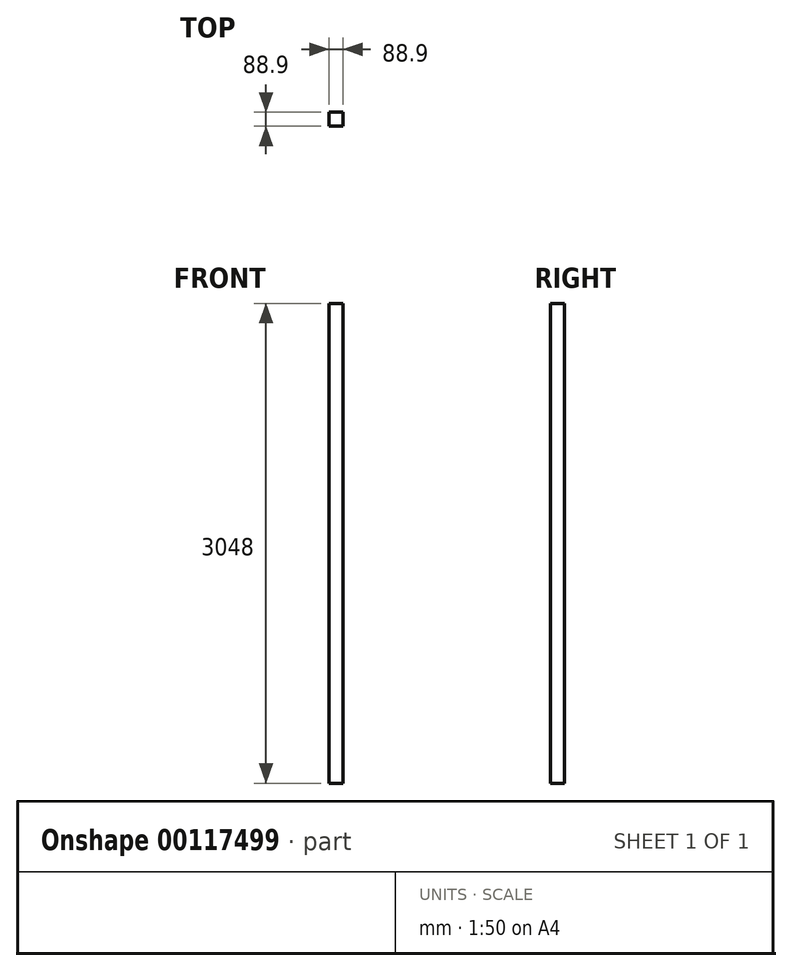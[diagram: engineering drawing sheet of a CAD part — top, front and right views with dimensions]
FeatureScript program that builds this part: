
annotation { "Feature Type Name" : "Feature", "Feature Type Description" : "" }
export const myFeature = defineFeature(function(context is Context, id is Id, definition is map)
    precondition{}
    {
        {
            var Q0;
            Q0=qCreatedBy(makeId("Top.planeOp"),FACE);
            var sketch = newSketch(context, id + "F0", { "sketchPlane" : qUnion([Q0])});
            skLineSegment(sketch, "E0.bottom", {"start": v(0, 0) * mm, "end": v(88.9, 0) * mm});
            skLineSegment(sketch, "E0.top", {"start": v(0, 88.9) * mm, "end": v(88.9, 88.9) * mm});
            skLineSegment(sketch, "E0.left", {"start": v(0, 0) * mm, "end": v(0, 88.9) * mm});
            skLineSegment(sketch, "E0.right", {"start": v(88.9, 0) * mm, "end": v(88.9, 88.9) * mm});
            skSolve(sketch);
        }
        {
            var Q0;
            Q0=makeQuery(id+"F0.imprint","IMPRINT",FACE,{"disambiguationData":[TD([[makeQuery(id+"F0.imprint","IMPRINT",EDGE,{"derivedFrom":sQuery(id+"F0.wireOp",EDGE,"E0.bottom")}),1.0]])]});
            extrude(context, id + "F1", {"entities" : qUnion([Q0]), "depth" : 3048 * mm});
        }
        {
            var Q0;
            Q0=qCreatedBy(makeId("Front.planeOp"),FACE);
            var sketch = newSketch(context, id + "F2", { "sketchPlane" : qUnion([Q0])});
            skLineSegment(sketch, "E1.bottom", {"start": v(-127.54, 0) * mm, "end": v(-165.64, 0) * mm});
            skLineSegment(sketch, "E1.top", {"start": v(-127.54, 184.15) * mm, "end": v(-165.64, 184.15) * mm});
            skLineSegment(sketch, "E1.left", {"start": v(-127.54, 0) * mm, "end": v(-127.54, 184.15) * mm});
            skLineSegment(sketch, "E1.right", {"start": v(-165.64, 0) * mm, "end": v(-165.64, 184.15) * mm});
            skSolve(sketch);
        }
        {
            var Q0;
            Q0=makeQuery(id+"F2.imprint","IMPRINT",FACE,{"disambiguationData":[TD([[makeQuery(id+"F2.imprint","IMPRINT",EDGE,{"derivedFrom":sQuery(id+"F2.wireOp",EDGE,"E1.bottom")}),-1.0]])]});
            extrude(context, id + "F3", {"entities" : qUnion([Q0]), "depth" : 2362.2 * mm});
        }
        {
            var Q0;
            Q0=qCreatedBy(makeId("Right.planeOp"),FACE);
            var sketch = newSketch(context, id + "F4", { "sketchPlane" : qUnion([Q0])});
            skLineSegment(sketch, "E2.bottom", {"start": v(230.04, 0) * mm, "end": v(268.14, 0) * mm});
            skLineSegment(sketch, "E2.top", {"start": v(230.04, 184.15) * mm, "end": v(268.14, 184.15) * mm});
            skLineSegment(sketch, "E2.left", {"start": v(230.04, 0) * mm, "end": v(230.04, 184.15) * mm});
            skLineSegment(sketch, "E2.right", {"start": v(268.14, 0) * mm, "end": v(268.14, 184.15) * mm});
            skSolve(sketch);
        }
        {
            var Q0;
            Q0=makeQuery(id+"F4.imprint","IMPRINT",FACE,{"disambiguationData":[TD([[makeQuery(id+"F4.imprint","IMPRINT",EDGE,{"derivedFrom":sQuery(id+"F4.wireOp",EDGE,"E2.bottom")}),1.0]])]});
            extrude(context, id + "F5", {"entities" : qUnion([Q0]), "depth" : 1200.15 * mm});
        }
        {
            var Q0;
            Q0=qCreatedBy(makeId("Front.planeOp"),FACE);
            var sketch = newSketch(context, id + "F6", { "sketchPlane" : qUnion([Q0])});
            skLineSegment(sketch, "E3.bottom", {"start": v(-315.67, 0) * mm, "end": v(-353.77, 0) * mm});
            skLineSegment(sketch, "E3.top", {"start": v(-315.67, 88.9) * mm, "end": v(-353.77, 88.9) * mm});
            skLineSegment(sketch, "E3.left", {"start": v(-315.67, 0) * mm, "end": v(-315.67, 88.9) * mm});
            skLineSegment(sketch, "E3.right", {"start": v(-353.77, 0) * mm, "end": v(-353.77, 88.9) * mm});
            skSolve(sketch);
        }
        {
            var Q0;
            Q0=makeQuery(id+"F6.imprint","IMPRINT",FACE,{"disambiguationData":[TD([[makeQuery(id+"F6.imprint","IMPRINT",EDGE,{"derivedFrom":sQuery(id+"F6.wireOp",EDGE,"E3.bottom")}),-1.0]])]});
            extrude(context, id + "F7", {"entities" : qUnion([Q0]), "depth" : 1123.95 * mm});
        }
        {
            var Q0;
            Q0=qCreatedBy(makeId("Top.planeOp"),FACE);
            var sketch = newSketch(context, id + "F8", { "sketchPlane" : qUnion([Q0])});
            skLineSegment(sketch, "E4.bottom", {"start": v(73.45, -206.98) * mm, "end": v(35.35, -206.98) * mm});
            skLineSegment(sketch, "E4.top", {"start": v(73.45, -118.08) * mm, "end": v(35.35, -118.08) * mm});
            skLineSegment(sketch, "E4.left", {"start": v(73.45, -206.98) * mm, "end": v(73.45, -118.08) * mm});
            skLineSegment(sketch, "E4.right", {"start": v(35.35, -206.98) * mm, "end": v(35.35, -118.08) * mm});
            skSolve(sketch);
        }
        {
            var Q0;
            Q0=makeQuery(id+"F8.imprint","IMPRINT",FACE,{"disambiguationData":[TD([[makeQuery(id+"F8.imprint","IMPRINT",EDGE,{"derivedFrom":sQuery(id+"F8.wireOp",EDGE,"E4.bottom")}),-1.0]])]});
            extrude(context, id + "F9", {"entities" : qUnion([Q0]), "depth" : 1320.8 * mm});
        }
        {
            var Q0;
            Q0=makeQuery(id+"F3.opExtrude","SWEPT_BODY",BODY,{"disambiguationData":[OSD([sQuery(id+"F2.wireOp",EDGE,"E1.bottom"),sQuery(id+"F2.wireOp",EDGE,"E1.top"),sQuery(id+"F2.wireOp",EDGE,"E1.left"),sQuery(id+"F2.wireOp",EDGE,"E1.right")])]});
            deleteBodies(context, id + "F10", {"entities" : qUnion([Q0])});
        }
        {
            var Q0;
            Q0=makeQuery(id+"F7.opExtrude","SWEPT_BODY",BODY,{"disambiguationData":[OSD([sQuery(id+"F6.wireOp",EDGE,"E3.bottom"),sQuery(id+"F6.wireOp",EDGE,"E3.top"),sQuery(id+"F6.wireOp",EDGE,"E3.left"),sQuery(id+"F6.wireOp",EDGE,"E3.right")])]});
            deleteBodies(context, id + "F11", {"entities" : qUnion([Q0])});
        }
        {
            var Q0;
            Q0=makeQuery(id+"F5.opExtrude","SWEPT_BODY",BODY,{"disambiguationData":[OSD([sQuery(id+"F4.wireOp",EDGE,"E2.bottom"),sQuery(id+"F4.wireOp",EDGE,"E2.top"),sQuery(id+"F4.wireOp",EDGE,"E2.left"),sQuery(id+"F4.wireOp",EDGE,"E2.right")])]});
            deleteBodies(context, id + "F12", {"entities" : qUnion([Q0])});
        }
        {
            var Q0;
            Q0=makeQuery(id+"F9.opExtrude","SWEPT_BODY",BODY,{"disambiguationData":[OSD([sQuery(id+"F8.wireOp",EDGE,"E4.bottom"),sQuery(id+"F8.wireOp",EDGE,"E4.top"),sQuery(id+"F8.wireOp",EDGE,"E4.left"),sQuery(id+"F8.wireOp",EDGE,"E4.right")])]});
            deleteBodies(context, id + "F13", {"entities" : qUnion([Q0])});
        }
    });
